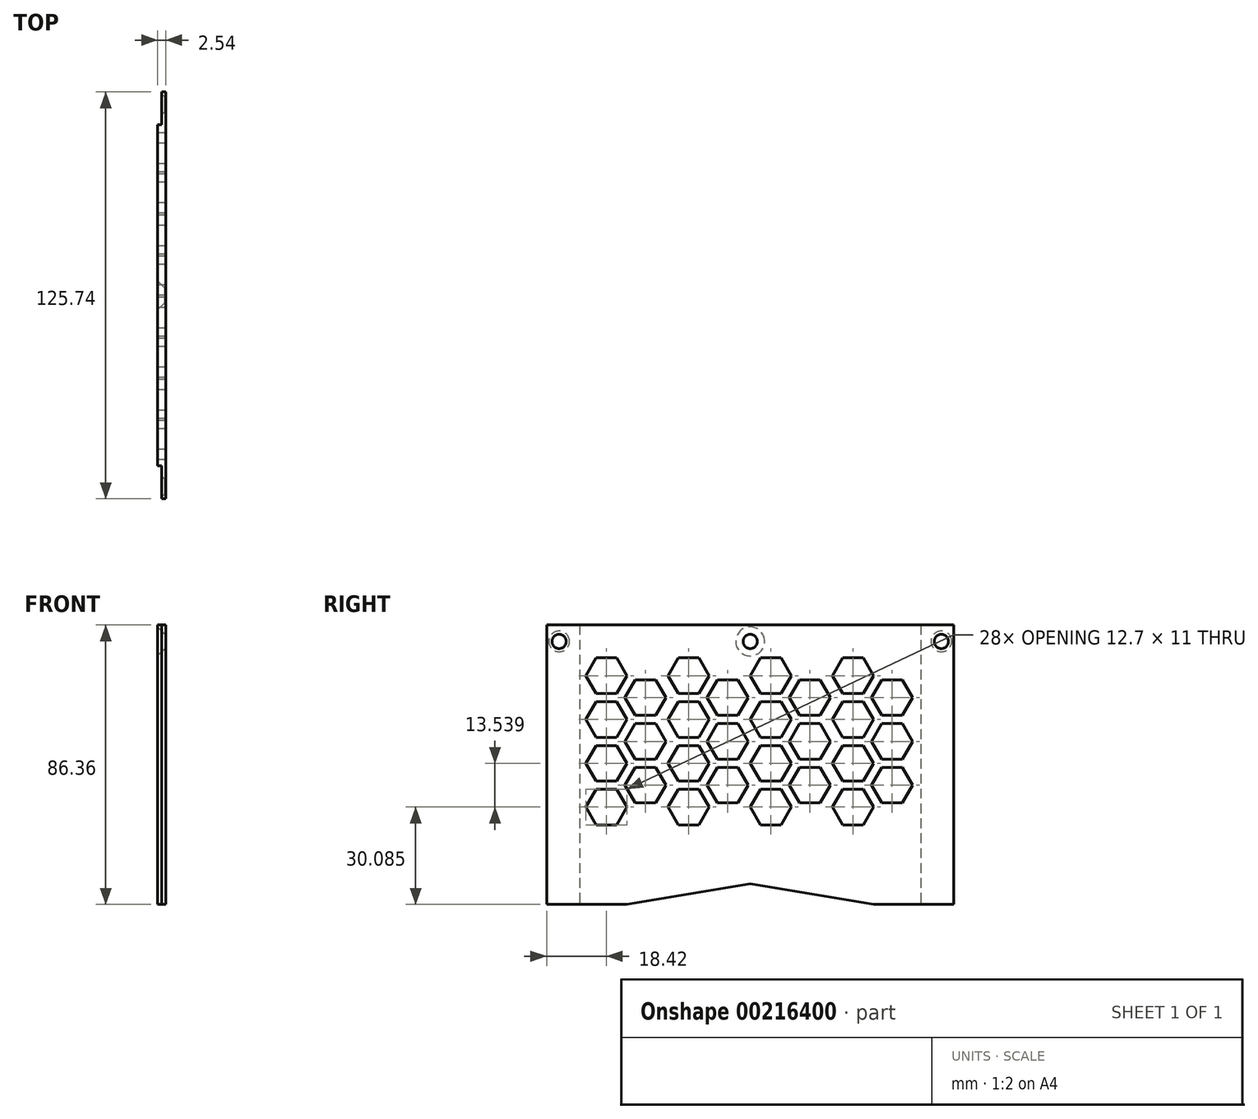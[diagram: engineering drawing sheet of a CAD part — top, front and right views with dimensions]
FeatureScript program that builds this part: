
annotation { "Feature Type Name" : "Feature", "Feature Type Description" : "" }
export const myFeature = defineFeature(function(context is Context, id is Id, definition is map)
    precondition{}
    {
        {
            var Q0;
            Q0=qCreatedBy(makeId("Right.planeOp"),FACE);
            var sketch = newSketch(context, id + "F0", { "sketchPlane" : qUnion([Q0])});
            skLineSegment(sketch, "E0.bottom", {"start": v(-62.87, 0) * mm, "end": v(62.87, 0) * mm});
            skLineSegment(sketch, "E0.top", {"start": v(-62.87, -86.36) * mm, "end": v(62.87, -86.36) * mm});
            skLineSegment(sketch, "E0.left", {"start": v(-62.87, 0) * mm, "end": v(-62.87, -86.36) * mm});
            skLineSegment(sketch, "E0.right", {"start": v(62.87, 0) * mm, "end": v(62.87, -86.36) * mm});
            skLineSegment(sketch, "E1", {"start": v(-62.87, 0) * mm, "end": v(-60.33, -86.36) * mm});
            skLineSegment(sketch, "E2", {"start": v(62.87, 0) * mm, "end": v(60.32, -86.36) * mm});
            skSolve(sketch);
        }
        {
            var Q0;
            Q0=makeQuery(id+"F0.imprint","IMPRINT",FACE,{"disambiguationData":[TD([[makeQuery(id+"F0.imprint","IMPRINT",EDGE,{"derivedFrom":sQuery(id+"F0.wireOp",EDGE,"E0.bottom")}),-1.0]])]});
            var Q1;
            {var subQ0=sQuery(id+"F0.wireOp",EDGE,"E0.left");Q1=makeQuery(id+"F0.imprint","IMPRINT",FACE,{"disambiguationData":[TD([[makeQuery(id+"F0.imprint","IMPRINT",EDGE,{"derivedFrom":subQ0}),1.0]])]});}
            var Q2;
            {var subQ0=sQuery(id+"F0.wireOp",EDGE,"E0.right");Q2=makeQuery(id+"F0.imprint","IMPRINT",FACE,{"disambiguationData":[TD([[makeQuery(id+"F0.imprint","IMPRINT",EDGE,{"derivedFrom":subQ0}),-1.0]])]});}
            extrude(context, id + "F1", {"entities" : qUnion([Q0, Q1, Q2]), "depth" : 2.54 * mm});
        }
        {
            var Q0;
            Q0=makeQuery(id+"F1.opExtrude","CAP_FACE",FACE,{"disambiguationData":[OSD([sQuery(id+"F0.wireOp",EDGE,"E0.bottom"),sQuery(id+"F0.wireOp",EDGE,"E0.top"),sQuery(id+"F0.wireOp",EDGE,"E0.left"),sQuery(id+"F0.wireOp",EDGE,"E0.right")])],"isStart":true});
            var sketch = newSketch(context, id + "F2", { "sketchPlane" : qUnion([Q0])});
            skPoint(sketch, "E3", {"position": v(-59.06, -5.08) * mm});
            skPoint(sketch, "E4", {"position": v(0, -5.08) * mm});
            skPoint(sketch, "E5", {"position": v(59.06, -5.08) * mm});
            skSolve(sketch);
        }
        {
            var Q0;
            Q0=sQuery(id+"F2.wireOp",VERTEX,"E3");
            var Q1;
            Q1=sQuery(id+"F2.wireOp",VERTEX,"E4");
            var Q2;
            Q2=sQuery(id+"F2.wireOp",VERTEX,"E5");
            var Q3;
            Q3=makeQuery(id+"F1.opExtrude","SWEPT_BODY",BODY,{"disambiguationData":[OSD([sQuery(id+"F0.wireOp",EDGE,"E0.bottom"),sQuery(id+"F0.wireOp",EDGE,"E0.top"),sQuery(id+"F0.wireOp",EDGE,"E0.left"),sQuery(id+"F0.wireOp",EDGE,"E0.right")])]});
            hole(context, id + "F3", {"style" : HoleStyle.C_SINK, "endStyle" : HoleEndStyle.BLIND, "standardTappedOrClearance" : lookupTablePath({ "standard" : "ISO", "fit" : "Normal", "size" : "M4", "type" : "Clearance" }), "standardBlindInLast" : lookupTablePath({ "fit" : "Standard", "standard" : "ISO", "size" : "M4", "type" : "Clearance" }), "holeDiameter" : 4.4 * mm, "cSinkDiameter" : 8.96 * mm, "cSinkAngle" : 90 * degree, "holeDepth" : 37.19 * mm, "tappedDepth" : 34.92 * mm, "tapClearance" : 3, "locations" : qUnion([Q0, Q1, Q2]), "scope" : qUnion([Q3])});
        }
        {
            var Q0;
            Q0=makeQuery(id+"F1.opExtrude","CAP_FACE",FACE,{"disambiguationData":[OSD([sQuery(id+"F0.wireOp",EDGE,"E0.bottom"),sQuery(id+"F0.wireOp",EDGE,"E0.top"),sQuery(id+"F0.wireOp",EDGE,"E0.left"),sQuery(id+"F0.wireOp",EDGE,"E0.right")])],"isStart":true});
            var sketch = newSketch(context, id + "F4", { "sketchPlane" : qUnion([Q0])});
            skLineSegment(sketch, "E6", {"start": v(-52.7, 0) * mm, "end": v(-52.7, -86.36) * mm});
            skLineSegment(sketch, "E7", {"start": v(-52.7, -86.36) * mm, "end": v(-78.84, -86.36) * mm});
            skLineSegment(sketch, "E8", {"start": v(-78.84, -86.36) * mm, "end": v(-78.84, 0) * mm});
            skLineSegment(sketch, "E9", {"start": v(-78.84, 0) * mm, "end": v(-52.7, 0) * mm});
            skLineSegment(sketch, "E10.MirrorCS", {"start": v(52.7, 0) * mm, "end": v(52.7, -86.36) * mm});
            skLineSegment(sketch, "E11.MirrorCS", {"start": v(78.84, 0) * mm, "end": v(52.7, 0) * mm});
            skLineSegment(sketch, "E12.MirrorCS", {"start": v(78.84, -86.36) * mm, "end": v(78.84, 0) * mm});
            skLineSegment(sketch, "E13.MirrorCS", {"start": v(52.7, -86.36) * mm, "end": v(78.84, -86.36) * mm});
            skSolve(sketch);
        }
        {
            var Q0;
            Q0 = qSketchRegion(id + "F4", true);
            extrude(context, id + "F5", {"entities" : qUnion([Q0]), "operationType" : NewBodyOperationType.REMOVE, "oppositeDirection" : true, "depth" : 1.27 * mm});
        }
        {
            var Q0;
            Q0=makeQuery(id+"F1.opExtrude","CAP_FACE",FACE,{"disambiguationData":[OSD([sQuery(id+"F0.wireOp",EDGE,"E0.bottom"),sQuery(id+"F0.wireOp",EDGE,"E0.top"),sQuery(id+"F0.wireOp",EDGE,"E0.left"),sQuery(id+"F0.wireOp",EDGE,"E0.right")])],"isStart":true});
            var sketch = newSketch(context, id + "F6", { "sketchPlane" : qUnion([Q0])});
            skLineSegment(sketch, "E14", {"start": v(-38.1, -86.36) * mm, "end": v(0, -80.01) * mm});
            skLineSegment(sketch, "E15", {"start": v(0, -80.01) * mm, "end": v(38.1, -86.36) * mm});
            skLineSegment(sketch, "E16", {"start": v(-38.1, -86.36) * mm, "end": v(38.1, -86.36) * mm});
            skCircle(sketch, "E17.cCircle", {"center": v(-43.82, -22.43) * mm, "radius": 5.5 * mm, "construction": true});
            skLineSegment(sketch, "E17.0", {"start": v(-47, -16.93) * mm, "end": v(-40.64, -16.93) * mm});
            skLineSegment(sketch, "E17.1", {"start": v(-40.64, -16.93) * mm, "end": v(-37.47, -22.43) * mm});
            skLineSegment(sketch, "E17.2", {"start": v(-37.47, -22.43) * mm, "end": v(-40.64, -27.93) * mm});
            skLineSegment(sketch, "E17.3", {"start": v(-40.64, -27.93) * mm, "end": v(-47, -27.93) * mm});
            skLineSegment(sketch, "E17.4", {"start": v(-47, -27.93) * mm, "end": v(-50.17, -22.43) * mm});
            skLineSegment(sketch, "E17.5", {"start": v(-50.17, -22.43) * mm, "end": v(-47, -16.93) * mm});
            skPoint(sketch, "E17.0.midPoint", {"position": v(-43.82, -16.93) * mm});
            skCircle(sketch, "E18.cCircle", {"center": v(-43.82, -35.97) * mm, "radius": 5.5 * mm, "construction": true});
            skLineSegment(sketch, "E18.0", {"start": v(-47, -30.47) * mm, "end": v(-40.64, -30.47) * mm});
            skLineSegment(sketch, "E18.1", {"start": v(-40.64, -30.47) * mm, "end": v(-37.47, -35.97) * mm});
            skLineSegment(sketch, "E18.2", {"start": v(-37.47, -35.97) * mm, "end": v(-40.64, -41.47) * mm});
            skLineSegment(sketch, "E18.3", {"start": v(-40.64, -41.47) * mm, "end": v(-47, -41.47) * mm});
            skLineSegment(sketch, "E18.4", {"start": v(-47, -41.47) * mm, "end": v(-50.16, -35.97) * mm});
            skLineSegment(sketch, "E18.5", {"start": v(-50.16, -35.97) * mm, "end": v(-47, -30.47) * mm});
            skPoint(sketch, "E18.0.midPoint", {"position": v(-43.82, -30.47) * mm});
            skCircle(sketch, "E19.cCircle", {"center": v(-43.82, -49.5) * mm, "radius": 5.5 * mm, "construction": true});
            skLineSegment(sketch, "E19.0", {"start": v(-47, -44) * mm, "end": v(-40.64, -44) * mm});
            skLineSegment(sketch, "E19.1", {"start": v(-40.64, -44) * mm, "end": v(-37.47, -49.5) * mm});
            skLineSegment(sketch, "E19.2", {"start": v(-39.05, -52.26) * mm, "end": v(-40.64, -55) * mm});
            skLineSegment(sketch, "E19.3", {"start": v(-40.64, -55) * mm, "end": v(-47, -55) * mm});
            skLineSegment(sketch, "E19.4", {"start": v(-47, -55) * mm, "end": v(-50.16, -49.5) * mm});
            skLineSegment(sketch, "E19.5", {"start": v(-50.16, -49.5) * mm, "end": v(-47, -44) * mm});
            skPoint(sketch, "E19.0.midPoint", {"position": v(-43.82, -44) * mm});
            skCircle(sketch, "E20.cCircle", {"center": v(-31.75, -42.74) * mm, "radius": 5.5 * mm, "construction": true});
            skLineSegment(sketch, "E20.0", {"start": v(-38.1, -42.74) * mm, "end": v(-34.93, -37.24) * mm});
            skLineSegment(sketch, "E20.1", {"start": v(-34.93, -37.24) * mm, "end": v(-28.58, -37.24) * mm});
            skLineSegment(sketch, "E20.2", {"start": v(-28.58, -37.24) * mm, "end": v(-25.4, -42.74) * mm});
            skLineSegment(sketch, "E20.3", {"start": v(-25.4, -42.74) * mm, "end": v(-28.58, -48.24) * mm});
            skLineSegment(sketch, "E20.4", {"start": v(-28.58, -48.24) * mm, "end": v(-34.93, -48.24) * mm});
            skLineSegment(sketch, "E20.5", {"start": v(-34.93, -48.24) * mm, "end": v(-38.1, -42.74) * mm});
            skPoint(sketch, "E20.0.midPoint", {"position": v(-36.51, -39.99) * mm});
            skCircle(sketch, "E21.cCircle", {"center": v(-31.75, -29.2) * mm, "radius": 5.5 * mm, "construction": true});
            skPoint(sketch, "E21.cCircle.centerSnap0", {"position": v(-31.75, -37.24) * mm});
            skLineSegment(sketch, "E21.0", {"start": v(-28.58, -34.7) * mm, "end": v(-34.93, -34.7) * mm});
            skLineSegment(sketch, "E21.1", {"start": v(-34.93, -34.7) * mm, "end": v(-38.1, -29.2) * mm});
            skLineSegment(sketch, "E21.2", {"start": v(-38.1, -29.2) * mm, "end": v(-34.93, -23.7) * mm});
            skLineSegment(sketch, "E21.3", {"start": v(-34.93, -23.7) * mm, "end": v(-28.58, -23.7) * mm});
            skLineSegment(sketch, "E21.4", {"start": v(-28.58, -23.7) * mm, "end": v(-25.4, -29.2) * mm});
            skLineSegment(sketch, "E21.5", {"start": v(-25.4, -29.2) * mm, "end": v(-28.58, -34.7) * mm});
            skPoint(sketch, "E21.0.midPoint", {"position": v(-31.75, -34.7) * mm});
            skCircle(sketch, "E22.cCircle", {"center": v(-31.75, -15.66) * mm, "radius": 5.5 * mm, "construction": true});
            skLineSegment(sketch, "E22.0", {"start": v(-28.58, -21.16) * mm, "end": v(-34.93, -21.16) * mm});
            skLineSegment(sketch, "E22.1", {"start": v(-34.93, -21.16) * mm, "end": v(-38.1, -15.66) * mm});
            skLineSegment(sketch, "E22.2", {"start": v(-38.1, -15.66) * mm, "end": v(-34.93, -10.16) * mm});
            skLineSegment(sketch, "E22.3", {"start": v(-34.93, -10.16) * mm, "end": v(-28.58, -10.16) * mm});
            skLineSegment(sketch, "E22.4", {"start": v(-28.58, -10.16) * mm, "end": v(-25.4, -15.66) * mm});
            skLineSegment(sketch, "E22.5", {"start": v(-25.4, -15.66) * mm, "end": v(-28.58, -21.16) * mm});
            skPoint(sketch, "E22.0.midPoint", {"position": v(-31.75, -21.16) * mm});
            skLineSegment(sketch, "E23", {"start": v(-39.05, -52.26) * mm, "end": v(-37.47, -49.5) * mm});
            skCircle(sketch, "E24.cCircle", {"center": v(-31.75, -56.27) * mm, "radius": 5.5 * mm, "construction": true});
            skLineSegment(sketch, "E24.0", {"start": v(-34.93, -50.78) * mm, "end": v(-28.58, -50.78) * mm});
            skLineSegment(sketch, "E24.1", {"start": v(-28.58, -50.78) * mm, "end": v(-25.4, -56.27) * mm});
            skLineSegment(sketch, "E24.2", {"start": v(-25.4, -56.27) * mm, "end": v(-28.58, -61.77) * mm});
            skLineSegment(sketch, "E24.3", {"start": v(-28.58, -61.77) * mm, "end": v(-34.93, -61.77) * mm});
            skLineSegment(sketch, "E24.4", {"start": v(-34.93, -61.77) * mm, "end": v(-38.1, -56.27) * mm});
            skLineSegment(sketch, "E24.5", {"start": v(-38.1, -56.27) * mm, "end": v(-34.93, -50.78) * mm});
            skPoint(sketch, "E24.0.midPoint", {"position": v(-31.75, -50.78) * mm});
            skLineSegment(sketch, "E25.1.0.0", {"start": v(-9.53, -34.7) * mm, "end": v(-12.7, -29.2) * mm});
            skPoint(sketch, "E25.1.0.1", {"position": v(-18.42, -30.47) * mm});
            skCircle(sketch, "E25.1.0.2", {"center": v(-6.35, -56.27) * mm, "radius": 5.5 * mm, "construction": true});
            skPoint(sketch, "E25.1.0.3", {"position": v(-6.35, -34.7) * mm});
            skLineSegment(sketch, "E25.1.0.4", {"start": v(-15.24, -30.47) * mm, "end": v(-12.07, -35.97) * mm});
            skLineSegment(sketch, "E25.1.0.5", {"start": v(-12.07, -35.97) * mm, "end": v(-15.24, -41.47) * mm});
            skLineSegment(sketch, "E25.1.0.6", {"start": v(0, -56.27) * mm, "end": v(-3.18, -61.77) * mm});
            skCircle(sketch, "E25.1.0.7", {"center": v(-18.42, -35.97) * mm, "radius": 5.5 * mm, "construction": true});
            skCircle(sketch, "E25.1.0.8", {"center": v(-18.42, -49.5) * mm, "radius": 5.5 * mm, "construction": true});
            skPoint(sketch, "E25.1.0.9", {"position": v(-18.42, -44) * mm});
            skLineSegment(sketch, "E25.1.0.10", {"start": v(-12.7, -15.66) * mm, "end": v(-9.53, -10.16) * mm});
            skLineSegment(sketch, "E25.1.0.11", {"start": v(-9.53, -61.77) * mm, "end": v(-12.7, -56.27) * mm});
            skLineSegment(sketch, "E25.1.0.12", {"start": v(-9.53, -23.7) * mm, "end": v(-3.18, -23.7) * mm});
            skLineSegment(sketch, "E25.1.0.13", {"start": v(-15.24, -44) * mm, "end": v(-12.07, -49.5) * mm});
            skPoint(sketch, "E25.1.0.14", {"position": v(-6.35, -50.78) * mm});
            skPoint(sketch, "E25.1.0.15", {"position": v(-6.35, -21.16) * mm});
            skCircle(sketch, "E25.1.0.16", {"center": v(-6.35, -42.74) * mm, "radius": 5.5 * mm, "construction": true});
            skLineSegment(sketch, "E25.1.0.17", {"start": v(-12.7, -29.2) * mm, "end": v(-9.53, -23.7) * mm});
            skLineSegment(sketch, "E25.1.0.18", {"start": v(-3.18, -61.77) * mm, "end": v(-9.53, -61.77) * mm});
            skLineSegment(sketch, "E25.1.0.19", {"start": v(-21.6, -55) * mm, "end": v(-24.76, -49.5) * mm});
            skPoint(sketch, "E25.1.0.20", {"position": v(-11.11, -39.99) * mm});
            skLineSegment(sketch, "E25.1.0.21", {"start": v(-3.18, -23.7) * mm, "end": v(0, -29.2) * mm});
            skCircle(sketch, "E25.1.0.22", {"center": v(-6.35, -15.66) * mm, "radius": 5.5 * mm, "construction": true});
            skCircle(sketch, "E25.1.0.23", {"center": v(-6.35, -29.2) * mm, "radius": 5.5 * mm, "construction": true});
            skLineSegment(sketch, "E25.1.0.24", {"start": v(-12.07, -22.43) * mm, "end": v(-15.24, -27.93) * mm});
            skLineSegment(sketch, "E25.1.0.25", {"start": v(-3.18, -50.78) * mm, "end": v(0, -56.27) * mm});
            skPoint(sketch, "E25.1.0.26", {"position": v(-6.35, -37.24) * mm});
            skPoint(sketch, "E25.1.0.27", {"position": v(-18.42, -16.93) * mm});
            skLineSegment(sketch, "E25.1.0.28", {"start": v(-9.53, -21.16) * mm, "end": v(-12.7, -15.66) * mm});
            skCircle(sketch, "E25.1.0.29", {"center": v(-18.42, -22.43) * mm, "radius": 5.5 * mm, "construction": true});
            skLineSegment(sketch, "E25.1.0.30", {"start": v(-24.76, -49.5) * mm, "end": v(-21.6, -44) * mm});
            skLineSegment(sketch, "E25.1.0.31", {"start": v(-15.24, -55) * mm, "end": v(-21.6, -55) * mm});
            skLineSegment(sketch, "E25.1.0.32", {"start": v(0, -29.2) * mm, "end": v(-3.18, -34.7) * mm});
            skLineSegment(sketch, "E25.1.0.33", {"start": v(-9.53, -48.24) * mm, "end": v(-12.7, -42.74) * mm});
            skLineSegment(sketch, "E25.1.0.34", {"start": v(-12.7, -42.74) * mm, "end": v(-9.53, -37.24) * mm});
            skLineSegment(sketch, "E25.1.0.35", {"start": v(-21.6, -30.47) * mm, "end": v(-15.24, -30.47) * mm});
            skLineSegment(sketch, "E25.1.0.36", {"start": v(-24.77, -22.43) * mm, "end": v(-21.6, -16.93) * mm});
            skLineSegment(sketch, "E25.1.0.37", {"start": v(-21.6, -44) * mm, "end": v(-15.24, -44) * mm});
            skLineSegment(sketch, "E25.1.0.38", {"start": v(-21.6, -27.93) * mm, "end": v(-24.77, -22.43) * mm});
            skLineSegment(sketch, "E25.1.0.39", {"start": v(-15.24, -27.93) * mm, "end": v(-21.6, -27.93) * mm});
            skLineSegment(sketch, "E25.1.0.40", {"start": v(-9.53, -37.24) * mm, "end": v(-3.18, -37.24) * mm});
            skLineSegment(sketch, "E25.1.0.41", {"start": v(-9.53, -10.16) * mm, "end": v(-3.18, -10.16) * mm});
            skLineSegment(sketch, "E25.1.0.42", {"start": v(-15.24, -41.47) * mm, "end": v(-21.6, -41.47) * mm});
            skLineSegment(sketch, "E25.1.0.43", {"start": v(-12.7, -56.27) * mm, "end": v(-9.53, -50.78) * mm});
            skLineSegment(sketch, "E25.1.0.44", {"start": v(-3.18, -48.24) * mm, "end": v(-9.53, -48.24) * mm});
            skLineSegment(sketch, "E25.1.0.45", {"start": v(-9.53, -50.78) * mm, "end": v(-3.18, -50.78) * mm});
            skLineSegment(sketch, "E25.1.0.46", {"start": v(0, -15.66) * mm, "end": v(-3.18, -21.16) * mm});
            skLineSegment(sketch, "E25.1.0.47", {"start": v(0, -42.74) * mm, "end": v(-3.18, -48.24) * mm});
            skLineSegment(sketch, "E25.1.0.48", {"start": v(-21.6, -41.47) * mm, "end": v(-24.76, -35.97) * mm});
            skLineSegment(sketch, "E25.1.0.49", {"start": v(-15.24, -16.93) * mm, "end": v(-12.07, -22.43) * mm});
            skLineSegment(sketch, "E25.1.0.50", {"start": v(-21.6, -16.93) * mm, "end": v(-15.24, -16.93) * mm});
            skLineSegment(sketch, "E25.1.0.51", {"start": v(-3.18, -34.7) * mm, "end": v(-9.53, -34.7) * mm});
            skLineSegment(sketch, "E25.1.0.52", {"start": v(-24.77, -35.97) * mm, "end": v(-21.6, -30.47) * mm});
            skLineSegment(sketch, "E25.1.0.53", {"start": v(-3.18, -21.16) * mm, "end": v(-9.53, -21.16) * mm});
            skLineSegment(sketch, "E25.1.0.54", {"start": v(-3.18, -10.16) * mm, "end": v(0, -15.66) * mm});
            skLineSegment(sketch, "E25.1.0.55", {"start": v(-3.18, -37.24) * mm, "end": v(0, -42.74) * mm});
            skLineSegment(sketch, "E25.1.0.56", {"start": v(-13.65, -52.26) * mm, "end": v(-12.07, -49.5) * mm});
            skLineSegment(sketch, "E25.1.0.57", {"start": v(-13.65, -52.26) * mm, "end": v(-15.24, -55) * mm});
            skLineSegment(sketch, "E25.2.0.0", {"start": v(15.87, -34.7) * mm, "end": v(12.7, -29.2) * mm});
            skPoint(sketch, "E25.2.0.1", {"position": v(6.98, -30.47) * mm});
            skCircle(sketch, "E25.2.0.2", {"center": v(19.05, -56.27) * mm, "radius": 5.5 * mm, "construction": true});
            skPoint(sketch, "E25.2.0.3", {"position": v(19.05, -34.7) * mm});
            skLineSegment(sketch, "E25.2.0.4", {"start": v(10.16, -30.47) * mm, "end": v(13.33, -35.97) * mm});
            skLineSegment(sketch, "E25.2.0.5", {"start": v(13.33, -35.97) * mm, "end": v(10.16, -41.47) * mm});
            skLineSegment(sketch, "E25.2.0.6", {"start": v(25.4, -56.27) * mm, "end": v(22.22, -61.77) * mm});
            skCircle(sketch, "E25.2.0.7", {"center": v(6.98, -35.97) * mm, "radius": 5.5 * mm, "construction": true});
            skCircle(sketch, "E25.2.0.8", {"center": v(6.98, -49.5) * mm, "radius": 5.5 * mm, "construction": true});
            skPoint(sketch, "E25.2.0.9", {"position": v(6.98, -44) * mm});
            skLineSegment(sketch, "E25.2.0.10", {"start": v(12.7, -15.66) * mm, "end": v(15.87, -10.16) * mm});
            skLineSegment(sketch, "E25.2.0.11", {"start": v(15.87, -61.77) * mm, "end": v(12.7, -56.27) * mm});
            skLineSegment(sketch, "E25.2.0.12", {"start": v(15.87, -23.7) * mm, "end": v(22.22, -23.7) * mm});
            skLineSegment(sketch, "E25.2.0.13", {"start": v(10.16, -44) * mm, "end": v(13.33, -49.5) * mm});
            skPoint(sketch, "E25.2.0.14", {"position": v(19.05, -50.78) * mm});
            skPoint(sketch, "E25.2.0.15", {"position": v(19.05, -21.16) * mm});
            skCircle(sketch, "E25.2.0.16", {"center": v(19.05, -42.74) * mm, "radius": 5.5 * mm, "construction": true});
            skLineSegment(sketch, "E25.2.0.17", {"start": v(12.7, -29.2) * mm, "end": v(15.87, -23.7) * mm});
            skLineSegment(sketch, "E25.2.0.18", {"start": v(22.22, -61.77) * mm, "end": v(15.87, -61.77) * mm});
            skLineSegment(sketch, "E25.2.0.19", {"start": v(3.8, -55) * mm, "end": v(0.64, -49.5) * mm});
            skPoint(sketch, "E25.2.0.20", {"position": v(14.29, -39.99) * mm});
            skLineSegment(sketch, "E25.2.0.21", {"start": v(22.22, -23.7) * mm, "end": v(25.4, -29.2) * mm});
            skCircle(sketch, "E25.2.0.22", {"center": v(19.05, -15.66) * mm, "radius": 5.5 * mm, "construction": true});
            skCircle(sketch, "E25.2.0.23", {"center": v(19.05, -29.2) * mm, "radius": 5.5 * mm, "construction": true});
            skLineSegment(sketch, "E25.2.0.24", {"start": v(13.33, -22.43) * mm, "end": v(10.16, -27.93) * mm});
            skLineSegment(sketch, "E25.2.0.25", {"start": v(22.22, -50.78) * mm, "end": v(25.4, -56.27) * mm});
            skPoint(sketch, "E25.2.0.26", {"position": v(19.05, -37.24) * mm});
            skPoint(sketch, "E25.2.0.27", {"position": v(6.98, -16.93) * mm});
            skLineSegment(sketch, "E25.2.0.28", {"start": v(15.87, -21.16) * mm, "end": v(12.7, -15.66) * mm});
            skCircle(sketch, "E25.2.0.29", {"center": v(6.98, -22.43) * mm, "radius": 5.5 * mm, "construction": true});
            skLineSegment(sketch, "E25.2.0.30", {"start": v(0.64, -49.5) * mm, "end": v(3.8, -44) * mm});
            skLineSegment(sketch, "E25.2.0.31", {"start": v(10.16, -55) * mm, "end": v(3.8, -55) * mm});
            skLineSegment(sketch, "E25.2.0.32", {"start": v(25.4, -29.2) * mm, "end": v(22.22, -34.7) * mm});
            skLineSegment(sketch, "E25.2.0.33", {"start": v(15.87, -48.24) * mm, "end": v(12.7, -42.74) * mm});
            skLineSegment(sketch, "E25.2.0.34", {"start": v(12.7, -42.74) * mm, "end": v(15.87, -37.24) * mm});
            skLineSegment(sketch, "E25.2.0.35", {"start": v(3.8, -30.47) * mm, "end": v(10.16, -30.47) * mm});
            skLineSegment(sketch, "E25.2.0.36", {"start": v(0.63, -22.43) * mm, "end": v(3.8, -16.93) * mm});
            skLineSegment(sketch, "E25.2.0.37", {"start": v(3.8, -44) * mm, "end": v(10.16, -44) * mm});
            skLineSegment(sketch, "E25.2.0.38", {"start": v(3.8, -27.93) * mm, "end": v(0.63, -22.43) * mm});
            skLineSegment(sketch, "E25.2.0.39", {"start": v(10.16, -27.93) * mm, "end": v(3.8, -27.93) * mm});
            skLineSegment(sketch, "E25.2.0.40", {"start": v(15.87, -37.24) * mm, "end": v(22.22, -37.24) * mm});
            skLineSegment(sketch, "E25.2.0.41", {"start": v(15.87, -10.16) * mm, "end": v(22.22, -10.16) * mm});
            skLineSegment(sketch, "E25.2.0.42", {"start": v(10.16, -41.47) * mm, "end": v(3.8, -41.47) * mm});
            skLineSegment(sketch, "E25.2.0.43", {"start": v(12.7, -56.27) * mm, "end": v(15.87, -50.78) * mm});
            skLineSegment(sketch, "E25.2.0.44", {"start": v(22.22, -48.24) * mm, "end": v(15.87, -48.24) * mm});
            skLineSegment(sketch, "E25.2.0.45", {"start": v(15.87, -50.78) * mm, "end": v(22.22, -50.78) * mm});
            skLineSegment(sketch, "E25.2.0.46", {"start": v(25.4, -15.66) * mm, "end": v(22.22, -21.16) * mm});
            skLineSegment(sketch, "E25.2.0.47", {"start": v(25.4, -42.74) * mm, "end": v(22.22, -48.24) * mm});
            skLineSegment(sketch, "E25.2.0.48", {"start": v(3.8, -41.47) * mm, "end": v(0.64, -35.97) * mm});
            skLineSegment(sketch, "E25.2.0.49", {"start": v(10.16, -16.93) * mm, "end": v(13.33, -22.43) * mm});
            skLineSegment(sketch, "E25.2.0.50", {"start": v(3.8, -16.93) * mm, "end": v(10.16, -16.93) * mm});
            skLineSegment(sketch, "E25.2.0.51", {"start": v(22.22, -34.7) * mm, "end": v(15.87, -34.7) * mm});
            skLineSegment(sketch, "E25.2.0.52", {"start": v(0.63, -35.97) * mm, "end": v(3.8, -30.47) * mm});
            skLineSegment(sketch, "E25.2.0.53", {"start": v(22.22, -21.16) * mm, "end": v(15.87, -21.16) * mm});
            skLineSegment(sketch, "E25.2.0.54", {"start": v(22.22, -10.16) * mm, "end": v(25.4, -15.66) * mm});
            skLineSegment(sketch, "E25.2.0.55", {"start": v(22.22, -37.24) * mm, "end": v(25.4, -42.74) * mm});
            skLineSegment(sketch, "E25.2.0.56", {"start": v(11.75, -52.26) * mm, "end": v(13.33, -49.5) * mm});
            skLineSegment(sketch, "E25.2.0.57", {"start": v(11.75, -52.26) * mm, "end": v(10.16, -55) * mm});
            skLineSegment(sketch, "E25.3.0.0", {"start": v(41.27, -34.7) * mm, "end": v(38.1, -29.2) * mm});
            skPoint(sketch, "E25.3.0.1", {"position": v(32.38, -30.47) * mm});
            skCircle(sketch, "E25.3.0.2", {"center": v(44.45, -56.27) * mm, "radius": 5.5 * mm, "construction": true});
            skPoint(sketch, "E25.3.0.3", {"position": v(44.45, -34.7) * mm});
            skLineSegment(sketch, "E25.3.0.4", {"start": v(35.56, -30.47) * mm, "end": v(38.73, -35.97) * mm});
            skLineSegment(sketch, "E25.3.0.5", {"start": v(38.73, -35.97) * mm, "end": v(35.56, -41.47) * mm});
            skLineSegment(sketch, "E25.3.0.6", {"start": v(50.8, -56.27) * mm, "end": v(47.62, -61.77) * mm});
            skCircle(sketch, "E25.3.0.7", {"center": v(32.38, -35.97) * mm, "radius": 5.5 * mm, "construction": true});
            skCircle(sketch, "E25.3.0.8", {"center": v(32.38, -49.5) * mm, "radius": 5.5 * mm, "construction": true});
            skPoint(sketch, "E25.3.0.9", {"position": v(32.38, -44) * mm});
            skLineSegment(sketch, "E25.3.0.10", {"start": v(38.1, -15.66) * mm, "end": v(41.27, -10.16) * mm});
            skLineSegment(sketch, "E25.3.0.11", {"start": v(41.27, -61.77) * mm, "end": v(38.1, -56.27) * mm});
            skLineSegment(sketch, "E25.3.0.12", {"start": v(41.27, -23.7) * mm, "end": v(47.62, -23.7) * mm});
            skLineSegment(sketch, "E25.3.0.13", {"start": v(35.56, -44) * mm, "end": v(38.73, -49.5) * mm});
            skPoint(sketch, "E25.3.0.14", {"position": v(44.45, -50.78) * mm});
            skPoint(sketch, "E25.3.0.15", {"position": v(44.45, -21.16) * mm});
            skCircle(sketch, "E25.3.0.16", {"center": v(44.45, -42.74) * mm, "radius": 5.5 * mm, "construction": true});
            skLineSegment(sketch, "E25.3.0.17", {"start": v(38.1, -29.2) * mm, "end": v(41.27, -23.7) * mm});
            skLineSegment(sketch, "E25.3.0.18", {"start": v(47.62, -61.77) * mm, "end": v(41.27, -61.77) * mm});
            skLineSegment(sketch, "E25.3.0.19", {"start": v(29.2, -55) * mm, "end": v(26.04, -49.5) * mm});
            skPoint(sketch, "E25.3.0.20", {"position": v(39.69, -39.99) * mm});
            skLineSegment(sketch, "E25.3.0.21", {"start": v(47.62, -23.7) * mm, "end": v(50.8, -29.2) * mm});
            skCircle(sketch, "E25.3.0.22", {"center": v(44.45, -15.66) * mm, "radius": 5.5 * mm, "construction": true});
            skCircle(sketch, "E25.3.0.23", {"center": v(44.45, -29.2) * mm, "radius": 5.5 * mm, "construction": true});
            skLineSegment(sketch, "E25.3.0.24", {"start": v(38.73, -22.43) * mm, "end": v(35.56, -27.93) * mm});
            skLineSegment(sketch, "E25.3.0.25", {"start": v(47.62, -50.78) * mm, "end": v(50.8, -56.27) * mm});
            skPoint(sketch, "E25.3.0.26", {"position": v(44.45, -37.24) * mm});
            skPoint(sketch, "E25.3.0.27", {"position": v(32.38, -16.93) * mm});
            skLineSegment(sketch, "E25.3.0.28", {"start": v(41.27, -21.16) * mm, "end": v(38.1, -15.66) * mm});
            skCircle(sketch, "E25.3.0.29", {"center": v(32.38, -22.43) * mm, "radius": 5.5 * mm, "construction": true});
            skLineSegment(sketch, "E25.3.0.30", {"start": v(26.04, -49.5) * mm, "end": v(29.2, -44) * mm});
            skLineSegment(sketch, "E25.3.0.31", {"start": v(35.56, -55) * mm, "end": v(29.2, -55) * mm});
            skLineSegment(sketch, "E25.3.0.32", {"start": v(50.8, -29.2) * mm, "end": v(47.62, -34.7) * mm});
            skLineSegment(sketch, "E25.3.0.33", {"start": v(41.27, -48.24) * mm, "end": v(38.1, -42.74) * mm});
            skLineSegment(sketch, "E25.3.0.34", {"start": v(38.1, -42.74) * mm, "end": v(41.27, -37.24) * mm});
            skLineSegment(sketch, "E25.3.0.35", {"start": v(29.2, -30.47) * mm, "end": v(35.56, -30.47) * mm});
            skLineSegment(sketch, "E25.3.0.36", {"start": v(26.03, -22.43) * mm, "end": v(29.2, -16.93) * mm});
            skLineSegment(sketch, "E25.3.0.37", {"start": v(29.2, -44) * mm, "end": v(35.56, -44) * mm});
            skLineSegment(sketch, "E25.3.0.38", {"start": v(29.2, -27.93) * mm, "end": v(26.03, -22.43) * mm});
            skLineSegment(sketch, "E25.3.0.39", {"start": v(35.56, -27.93) * mm, "end": v(29.2, -27.93) * mm});
            skLineSegment(sketch, "E25.3.0.40", {"start": v(41.27, -37.24) * mm, "end": v(47.62, -37.24) * mm});
            skLineSegment(sketch, "E25.3.0.41", {"start": v(41.27, -10.16) * mm, "end": v(47.62, -10.16) * mm});
            skLineSegment(sketch, "E25.3.0.42", {"start": v(35.56, -41.47) * mm, "end": v(29.2, -41.47) * mm});
            skLineSegment(sketch, "E25.3.0.43", {"start": v(38.1, -56.27) * mm, "end": v(41.27, -50.78) * mm});
            skLineSegment(sketch, "E25.3.0.44", {"start": v(47.62, -48.24) * mm, "end": v(41.27, -48.24) * mm});
            skLineSegment(sketch, "E25.3.0.45", {"start": v(41.27, -50.78) * mm, "end": v(47.62, -50.78) * mm});
            skLineSegment(sketch, "E25.3.0.46", {"start": v(50.8, -15.66) * mm, "end": v(47.62, -21.16) * mm});
            skLineSegment(sketch, "E25.3.0.47", {"start": v(50.8, -42.74) * mm, "end": v(47.62, -48.24) * mm});
            skLineSegment(sketch, "E25.3.0.48", {"start": v(29.2, -41.47) * mm, "end": v(26.03, -35.97) * mm});
            skLineSegment(sketch, "E25.3.0.49", {"start": v(35.56, -16.93) * mm, "end": v(38.73, -22.43) * mm});
            skLineSegment(sketch, "E25.3.0.50", {"start": v(29.2, -16.93) * mm, "end": v(35.56, -16.93) * mm});
            skLineSegment(sketch, "E25.3.0.51", {"start": v(47.62, -34.7) * mm, "end": v(41.27, -34.7) * mm});
            skLineSegment(sketch, "E25.3.0.52", {"start": v(26.03, -35.97) * mm, "end": v(29.2, -30.47) * mm});
            skLineSegment(sketch, "E25.3.0.53", {"start": v(47.62, -21.16) * mm, "end": v(41.27, -21.16) * mm});
            skLineSegment(sketch, "E25.3.0.54", {"start": v(47.62, -10.16) * mm, "end": v(50.8, -15.66) * mm});
            skLineSegment(sketch, "E25.3.0.55", {"start": v(47.62, -37.24) * mm, "end": v(50.8, -42.74) * mm});
            skLineSegment(sketch, "E25.3.0.56", {"start": v(37.15, -52.26) * mm, "end": v(38.73, -49.5) * mm});
            skLineSegment(sketch, "E25.3.0.57", {"start": v(37.15, -52.26) * mm, "end": v(35.56, -55) * mm});
            skLineSegment(sketch, "E25.direction1", {"start": v(-47, -55) * mm, "end": v(-21.6, -55) * mm, "construction": true});
            skSolve(sketch);
        }
        {
            var Q0;
            Q0 = qSketchRegion(id + "F6", true);
            extrude(context, id + "F7", {"entities" : qUnion([Q0]), "operationType" : NewBodyOperationType.REMOVE, "oppositeDirection" : true, "depth" : 25.4 * mm});
        }
    });
